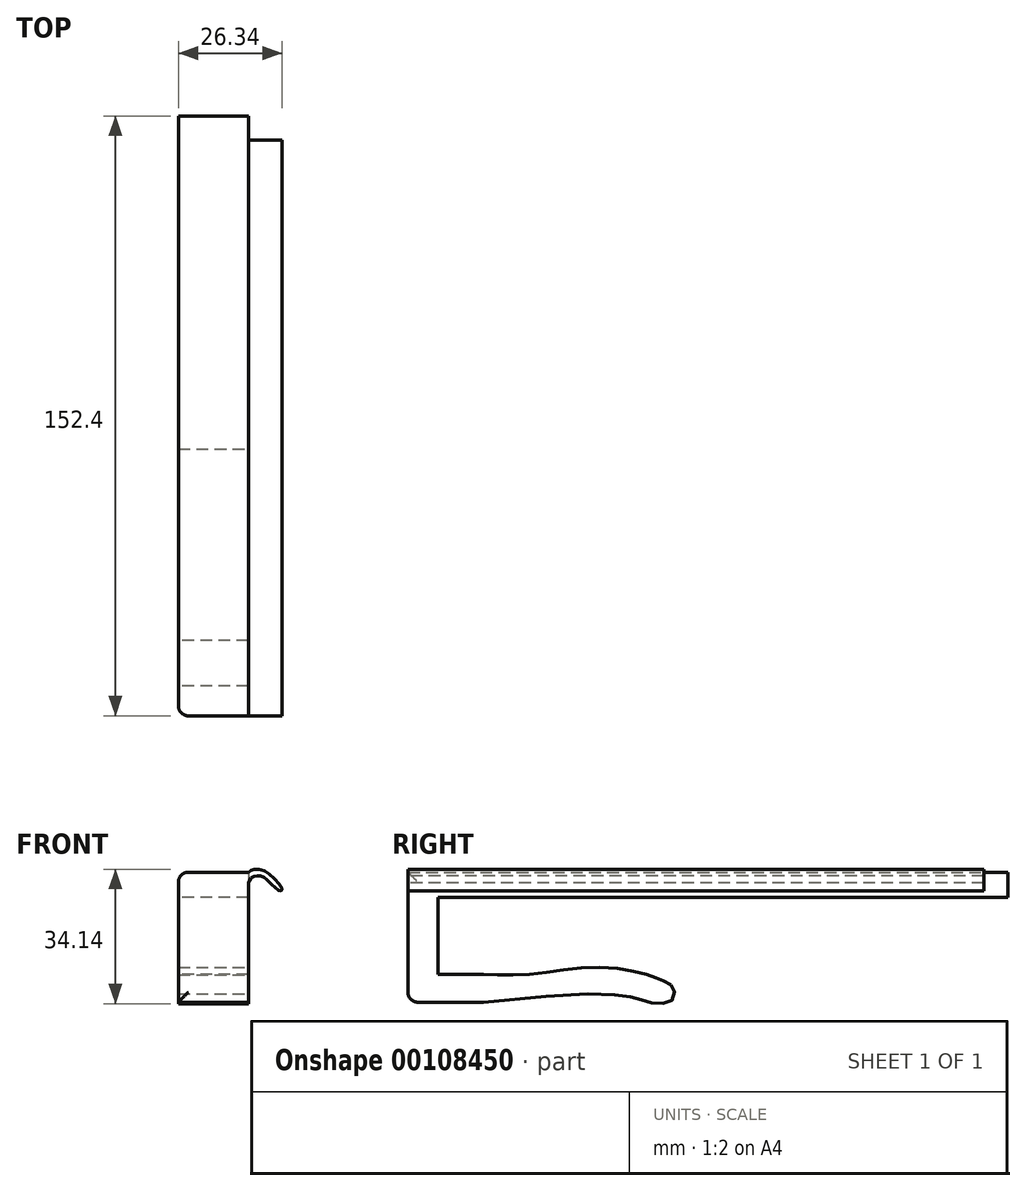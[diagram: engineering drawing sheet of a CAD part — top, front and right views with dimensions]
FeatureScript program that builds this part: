
annotation { "Feature Type Name" : "Feature", "Feature Type Description" : "" }
export const myFeature = defineFeature(function(context is Context, id is Id, definition is map)
    precondition{}
    {
        {
            var Q0;
            Q0=qCreatedBy(makeId("Right.planeOp"),FACE);
            var sketch = newSketch(context, id + "F0", { "sketchPlane" : qUnion([Q0])});
            skLineSegment(sketch, "E0.bottom", {"start": v(0, 0) * mm, "end": v(7.62, 0) * mm});
            skLineSegment(sketch, "E0.top", {"start": v(0, -33.02) * mm, "end": v(7.62, -33.02) * mm});
            skLineSegment(sketch, "E0.left", {"start": v(0, 0) * mm, "end": v(0, -33.02) * mm});
            skLineSegment(sketch, "E0.right", {"start": v(7.62, 0) * mm, "end": v(7.62, -33.02) * mm});
            skLineSegment(sketch, "E1.bottom", {"start": v(7.62, 0) * mm, "end": v(152.4, 0) * mm});
            skLineSegment(sketch, "E1.top", {"start": v(7.62, -6.35) * mm, "end": v(152.4, -6.35) * mm});
            skLineSegment(sketch, "E1.left", {"start": v(7.62, 0) * mm, "end": v(7.62, -6.35) * mm});
            skLineSegment(sketch, "E1.right", {"start": v(152.4, 0) * mm, "end": v(152.4, -6.35) * mm});
            skLineSegment(sketch, "E2.bottom", {"start": v(7.62, -25.9) * mm, "end": v(19.14, -25.9) * mm});
            skLineSegment(sketch, "E2.top", {"start": v(7.62, -33.02) * mm, "end": v(19.14, -33.02) * mm});
            skLineSegment(sketch, "E2.left", {"start": v(7.62, -25.9) * mm, "end": v(7.62, -33.02) * mm});
            skLineSegment(sketch, "E2.right", {"start": v(19.14, -25.9) * mm, "end": v(19.14, -33.02) * mm});
            skFitSpline(sketch, "E3", {"points": [v(19.14, -25.9) * mm, v(31.3, -25.9) * mm, v(47.04, -24.13) * mm, v(60.39, -25.9) * mm, v(64.5, -27.43) * mm, v(67.39, -29.26) * mm, v(66.98, -32.62) * mm, v(61.22, -33.02) * mm, v(19.14, -33.02) * mm], "startDerivative": vector(77.3, -2.63) * mm, "endDerivative": vector(-435.06, -48.4) * mm});
            skSolve(sketch);
        }
        {
            var Q0;
            Q0 = qSketchRegion(id + "F0", true);
            extrude(context, id + "F1", {"entities" : qUnion([Q0]), "depth" : 17.78 * mm});
        }
        {
            var Q0;
            Q0=makeQuery(id+"F1.opExtrude","SWEPT_FACE",FACE,{"disambiguationData":[OSD([sQuery(id+"F0.wireOp",EDGE,"E0.left")])]});
            var sketch = newSketch(context, id + "F2", { "sketchPlane" : qUnion([Q0])});
            skFitSpline(sketch, "E4", {"points": [v(17.78, 0) * mm, v(19.16, 0.65) * mm, v(20.1, 0.75) * mm, v(20.73, 0.67) * mm, v(22.36, 0) * mm, v(26.32, -4.16) * mm, v(25.94, -4.74) * mm, v(23.93, -3.27) * mm, v(22.46, -1.88) * mm, v(21.23, -1.06) * mm, v(19.46, -0.95) * mm, v(18.33, -1.6) * mm, v(17.78, -2.69) * mm, v(17.78, -3.07) * mm, v(17.78, -3.32) * mm], "startDerivative": vector(14.6, 13.94) * mm, "endDerivative": vector(-0.16, -3.23) * mm});
            skSolve(sketch);
        }
        {
            var Q0;
            {var subQ0=sQuery(id+"F2.wireOp",EDGE,"E4");var subQ1=sQuery(id+"F0.wireOp",EDGE,"E0.left");var subQ2=makeQuery(id+"F1.opExtrude","CAP_EDGE",EDGE,{"disambiguationData":[OSD([subQ1])],"isStart":false});var subQ4=makeQuery(id+"F2.imprint","INTERSECT",VERTEX,{"disambiguationData":[OD(1.0)],"derivedFrom":[subQ2,subQ0]});Q0=makeQuery(id+"F2.imprint","IMPRINT",FACE,{"disambiguationData":[TD([[makeQuery(id+"F2.imprint","IMPRINT",EDGE,{"disambiguationData":[TD([[subQ4,1.0]])],"derivedFrom":subQ0}),-1.0]])]});}
            extrude(context, id + "F3", {"entities" : qUnion([Q0]), "operationType" : NewBodyOperationType.ADD, "oppositeDirection" : true, "depth" : 146.25 * mm});
        }
        {
            var Q0;
            Q0=makeQuery(id+"F1.opExtrude","CAP_EDGE",EDGE,{"disambiguationData":[OSD([sQuery(id+"F0.wireOp",EDGE,"E0.bottom"),sQuery(id+"F0.wireOp",EDGE,"E1.bottom")])],"isStart":true});
            var Q1;
            Q1=makeQuery(id+"F1.opExtrude","SWEPT_EDGE",EDGE,{"disambiguationData":[OSD([sQuery(id+"F0.wireOp",EDGE,"E0.top"),sQuery(id+"F0.wireOp",EDGE,"E0.left")])]});
            var Q2;
            Q2=makeQuery(id+"F1.opExtrude","CAP_EDGE",EDGE,{"disambiguationData":[OSD([sQuery(id+"F0.wireOp",EDGE,"E0.left")])],"isStart":true});
            fillet(context, id + "F4", {"entities" : qUnion([Q0, Q1, Q2]), "radius" : 2.54 * mm, "tangentPropagation" : true, "allowEdgeOverflow" : false});
        }
    });
